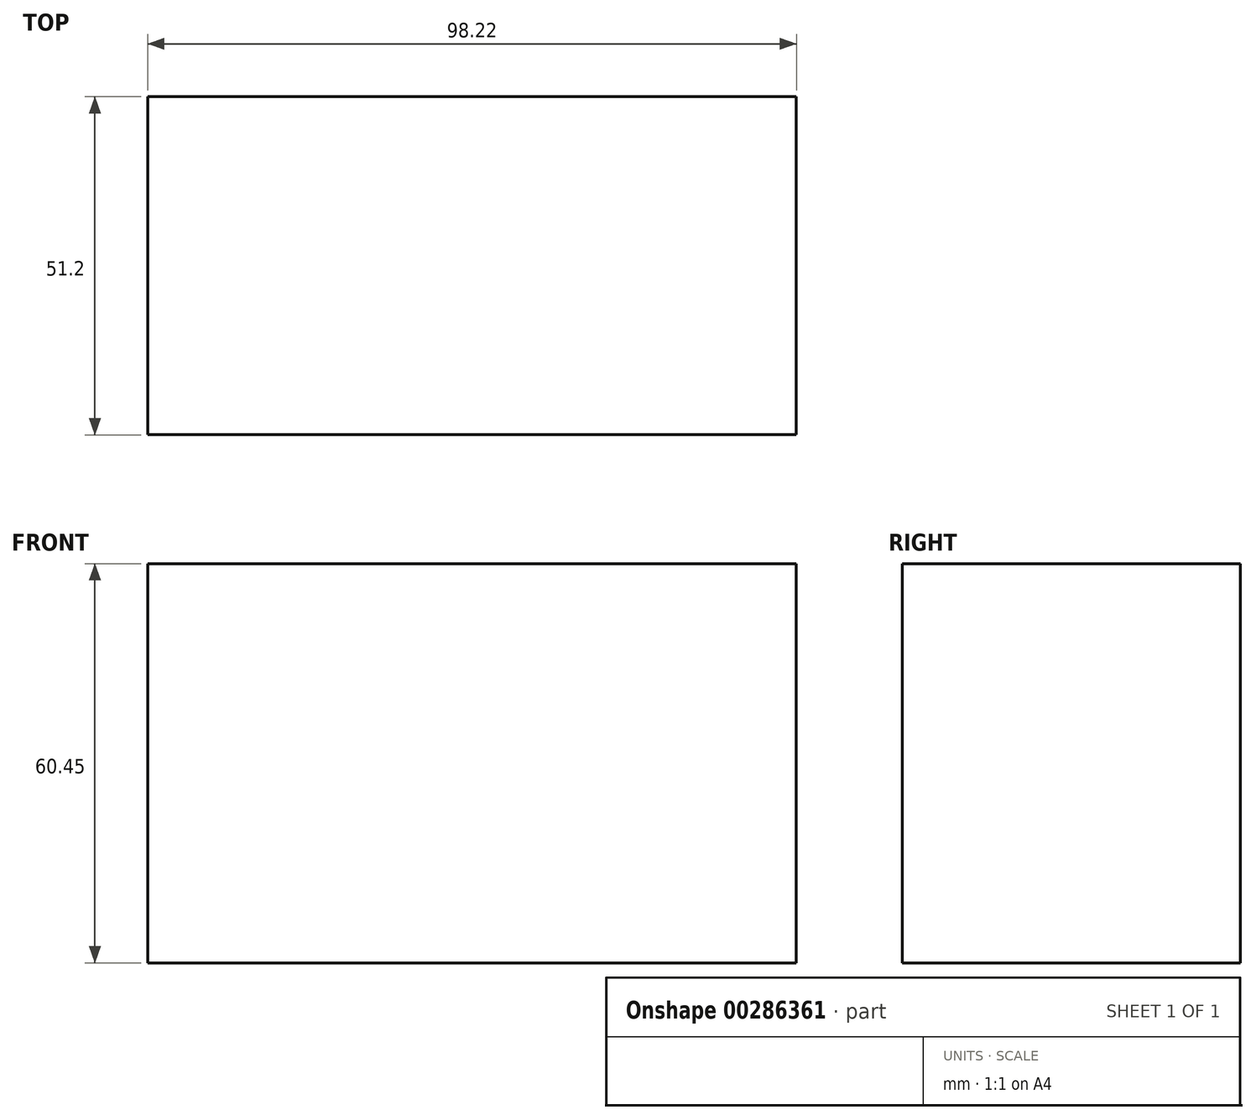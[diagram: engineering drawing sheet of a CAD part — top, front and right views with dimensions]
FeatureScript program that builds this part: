
annotation { "Feature Type Name" : "Feature", "Feature Type Description" : "" }
export const myFeature = defineFeature(function(context is Context, id is Id, definition is map)
    precondition{}
    {
        {
            var Q0;
            Q0=qCreatedBy(makeId("Top.planeOp"),FACE);
            var sketch = newSketch(context, id + "F0", { "sketchPlane" : qUnion([Q0])});
            skLineSegment(sketch, "E0.bottom", {"start": v(-49.1, 25.6) * mm, "end": v(49.1, 25.6) * mm});
            skLineSegment(sketch, "E0.top", {"start": v(-49.1, -25.6) * mm, "end": v(49.1, -25.6) * mm});
            skLineSegment(sketch, "E0.left", {"start": v(-49.1, 25.6) * mm, "end": v(-49.1, -25.6) * mm});
            skLineSegment(sketch, "E0.right", {"start": v(49.1, 25.6) * mm, "end": v(49.1, -25.6) * mm});
            skPoint(sketch, "E0.middle", {"position": v(0, 0) * mm});
            skSolve(sketch);
        }
        {
            var Q0;
            Q0 = qSketchRegion(id + "F0", true);
            extrude(context, id + "F1", {"entities" : qUnion([Q0]), "depth" : 60.45 * mm});
        }
    });
